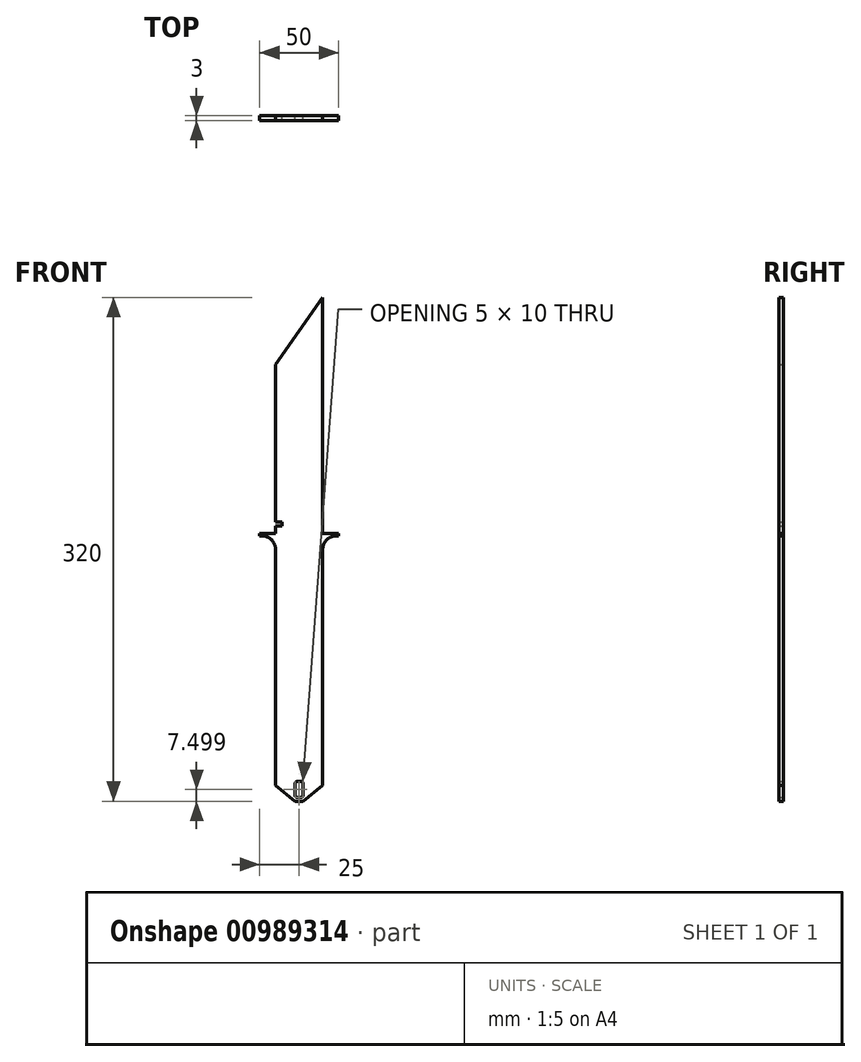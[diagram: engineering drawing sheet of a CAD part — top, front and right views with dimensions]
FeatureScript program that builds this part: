
annotation { "Feature Type Name" : "Feature", "Feature Type Description" : "" }
export const myFeature = defineFeature(function(context is Context, id is Id, definition is map)
    precondition{}
    {
        {
            var Q0;
            Q0=qCreatedBy(makeId("Front.planeOp"),FACE);
            var sketch = newSketch(context, id + "F0", { "sketchPlane" : qUnion([Q0])});
            skLineSegment(sketch, "E0", {"start": v(0, 237) * mm, "end": v(0, 87) * mm});
            skLineSegment(sketch, "E1", {"start": v(-30, 194.5) * mm, "end": v(0, 237) * mm});
            skPoint(sketch, "E2", {"position": v(0, 77) * mm});
            skLineSegment(sketch, "E3", {"start": v(0, 77) * mm, "end": v(0, -73) * mm});
            skLineSegment(sketch, "E4", {"start": v(10, 87) * mm, "end": v(0, 87) * mm});
            skLineSegment(sketch, "E5", {"start": v(-30, 77) * mm, "end": v(-30, -73) * mm});
            skLineSegment(sketch, "E6", {"start": v(-40, 87) * mm, "end": v(-30, 87) * mm});
            skLineSegment(sketch, "E7", {"start": v(-30, -73) * mm, "end": v(-17.5, -83) * mm});
            skLineSegment(sketch, "E8", {"start": v(-12.5, -83) * mm, "end": v(0, -73) * mm});
            skLineSegment(sketch, "E9", {"start": v(-17.5, -83) * mm, "end": v(-12.5, -83) * mm});
            skPoint(sketch, "E10.centerSnap0", {"position": v(-15, -83) * mm});
            skLineSegment(sketch, "E11", {"start": v(-13.5, -80.5) * mm, "end": v(-16.5, -80.5) * mm});
            skLineSegment(sketch, "E12", {"start": v(-17.5, -79.5) * mm, "end": v(-17.5, -71.5) * mm});
            skLineSegment(sketch, "E13", {"start": v(-16.5, -70.5) * mm, "end": v(-13.5, -70.5) * mm});
            skLineSegment(sketch, "E14", {"start": v(-12.5, -71.5) * mm, "end": v(-12.5, -79.5) * mm});
            skPoint(sketch, "E15.visualSharp", {"position": v(-17.5, -70.5) * mm});
            skArc(sketch, "E15.filletArc", {"start": v(-16.5, -70.5) * mm, "mid": v(-17.2, -70.78) * mm, "end": v(-17.5, -71.5) * mm});
            skPoint(sketch, "E16.visualSharp", {"position": v(-12.5, -70.5) * mm});
            skArc(sketch, "E16.filletArc", {"start": v(-12.5, -71.5) * mm, "mid": v(-12.8, -70.78) * mm, "end": v(-13.5, -70.5) * mm});
            skPoint(sketch, "E17.visualSharp", {"position": v(-12.5, -80.5) * mm});
            skArc(sketch, "E17.filletArc", {"start": v(-13.5, -80.5) * mm, "mid": v(-12.8, -80.2) * mm, "end": v(-12.5, -79.5) * mm});
            skPoint(sketch, "E18.visualSharp", {"position": v(-17.5, -80.5) * mm});
            skArc(sketch, "E18.filletArc", {"start": v(-17.5, -79.5) * mm, "mid": v(-17.2, -80.2) * mm, "end": v(-16.5, -80.5) * mm});
            skLineSegment(sketch, "E19", {"start": v(-30, 194.5) * mm, "end": v(-30, 94.5) * mm});
            skLineSegment(sketch, "E20", {"start": v(-30, 94.5) * mm, "end": v(-26, 94.5) * mm});
            skLineSegment(sketch, "E21", {"start": v(-26, 94.5) * mm, "end": v(-26, 92) * mm});
            skLineSegment(sketch, "E22", {"start": v(-26, 92) * mm, "end": v(-30, 92) * mm});
            skLineSegment(sketch, "E23", {"start": v(-30, 92) * mm, "end": v(-30, 87) * mm});
            skLineSegment(sketch, "E24", {"start": v(-40, 87) * mm, "end": v(-40, 85.5) * mm});
            skArc(sketch, "E25", {"start": v(-30, 77) * mm, "mid": v(-33.03, 83.57) * mm, "end": v(-40, 85.5) * mm});
            skLineSegment(sketch, "E26", {"start": v(10, 87) * mm, "end": v(10, 85.5) * mm});
            skArc(sketch, "E27", {"start": v(0, 77) * mm, "mid": v(3.04, 83.57) * mm, "end": v(10, 85.5) * mm});
            skSolve(sketch);
        }
        {
            var Q0;
            Q0=makeQuery(id+"F0.imprint","IMPRINT",FACE,{"disambiguationData":[TD([[makeQuery(id+"F0.imprint","IMPRINT",EDGE,{"derivedFrom":sQuery(id+"F0.wireOp",EDGE,"E0")}),-1.0]])]});
            extrude(context, id + "F1", {"entities" : qUnion([Q0]), "endBound" : BoundingType.SYMMETRIC, "depth" : 3 * mm, "offsetDistance" : 25 * mm});
        }
    });
